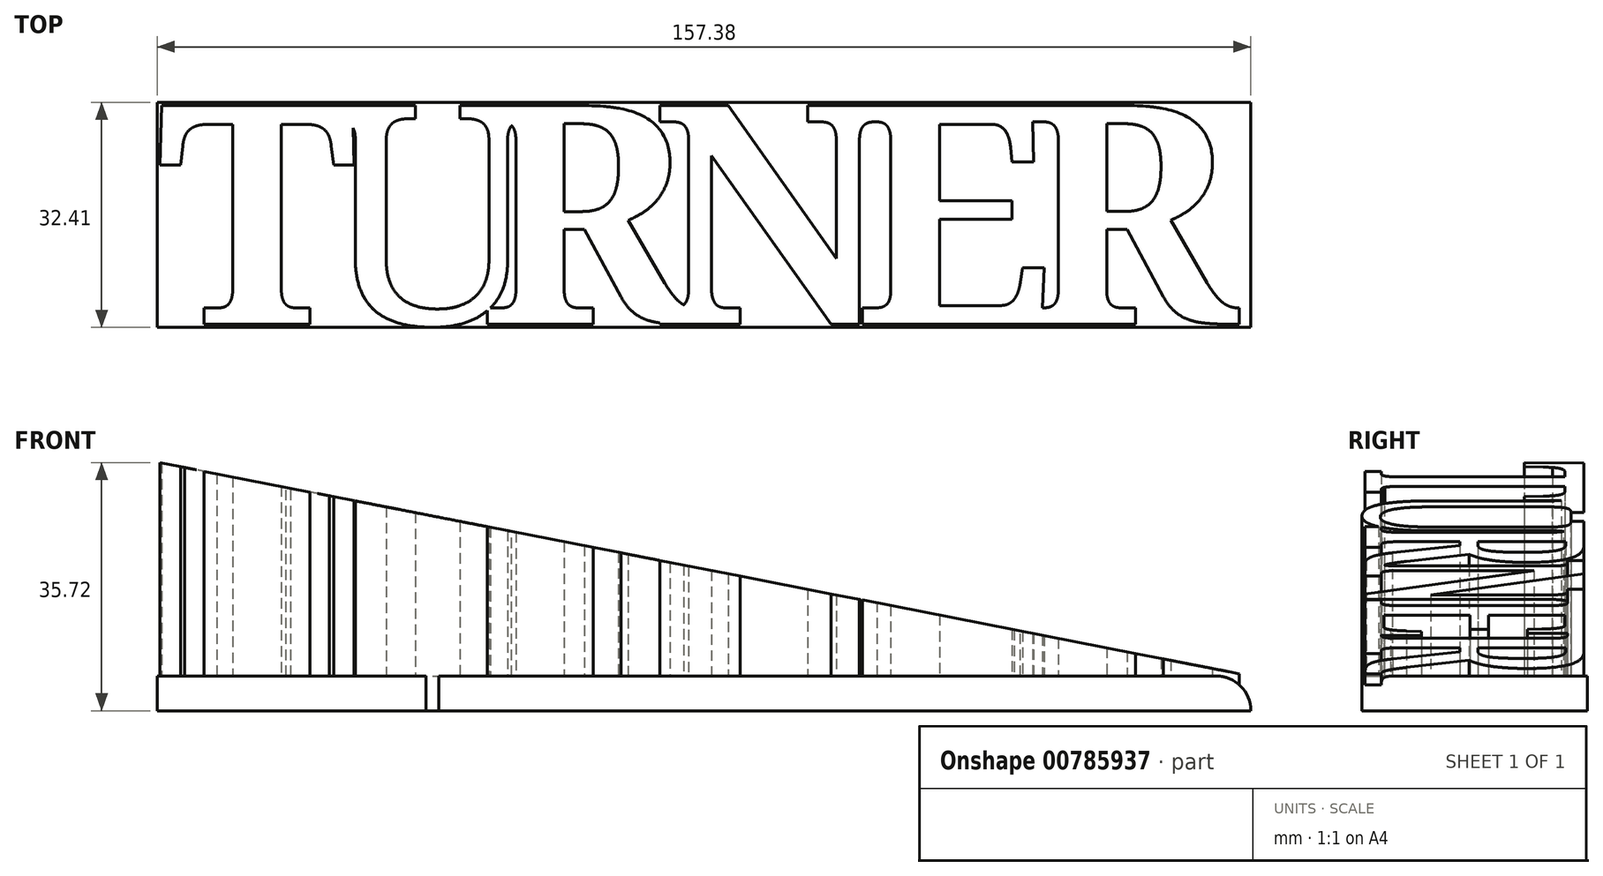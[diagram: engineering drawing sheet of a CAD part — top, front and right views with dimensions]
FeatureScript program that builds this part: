
annotation { "Feature Type Name" : "Feature", "Feature Type Description" : "" }
export const myFeature = defineFeature(function(context is Context, id is Id, definition is map)
    precondition{}
    {
        {
            var Q0;
            Q0=qCreatedBy(makeId("Top.planeOp"),FACE);
            var sketch = newSketch(context, id + "F0", { "sketchPlane" : qUnion([Q0])});
            skCircle(sketch, "E0", {"center": v(0, 0) * mm, "radius": 77 * mm, "construction": true});
            skText(sketch, "E1", { "text": "T", "fontName": "NotoSerif-Bold.ttf"});
            skText(sketch, "E2", { "text": "U", "fontName": "NotoSerif-Regular.ttf"});
            skText(sketch, "E3", { "text": "R", "fontName": "NotoSerif-Bold.ttf"});
            skText(sketch, "E4", { "text": "N", "fontName": "NotoSerif-Bold.ttf"});
            skText(sketch, "E5", { "text": "E", "fontName": "NotoSerif-Bold.ttf"});
            skText(sketch, "E6", { "text": "R", "fontName": "NotoSerif-Bold.ttf"});
            const initialGuessF0  = {"E1": [-0.07837, -0.01588, 1, 0, 0.03175], "E2": [-0.05468, -0.01588, 1, 0, 0.03175], "E3": [-0.03206, -0.01588, 1, 0, 0.03175], "E4": [-0.0072, -0.01588, 1, 0, 0.03175], "E5": [0.02189, -0.01587, 1, 0, 0.03175], "E6": [0.046, -0.01587, 1, 0, 0.03175]};
            skSetInitialGuess(sketch, initialGuessF0);
            skSolve(sketch);
        }
        {
            var Q0;
            Q0 = qSketchRegion(id + "F0", true);
            extrude(context, id + "F1", {"entities" : qUnion([Q0]), "depth" : 38.1 * mm, "offsetDistance" : 25 * mm});
        }
        {
            var Q0;
            Q0=qCreatedBy(makeId("Top.planeOp"),FACE);
            var sketch = newSketch(context, id + "F2", { "sketchPlane" : qUnion([Q0])});
            skLineSegment(sketch, "E7.bottom", {"start": v(-78.34, 16.1) * mm, "end": v(79.04, 16.1) * mm});
            skLineSegment(sketch, "E7.top", {"start": v(-78.34, -16.3) * mm, "end": v(79.04, -16.3) * mm});
            skLineSegment(sketch, "E7.left", {"start": v(-78.34, 16.1) * mm, "end": v(-78.34, -16.3) * mm});
            skLineSegment(sketch, "E7.right", {"start": v(79.04, 16.1) * mm, "end": v(79.04, -16.3) * mm});
            skSolve(sketch);
        }
        {
            var Q0;
            Q0 = qSketchRegion(id + "F2", true);
            extrude(context, id + "F3", {"entities" : qUnion([Q0]), "operationType" : NewBodyOperationType.ADD, "depth" : 5 * mm, "offsetDistance" : 25 * mm});
        }
        {
            var Q0;
            {var subQ2=sQuery(id+"F2.wireOp",EDGE,"E7.top");var subQ4=sQuery(id+"F0.wireOp",EDGE,"E2.sketch_text.stroke-45");Q0=makeQuery(id+"F3.boolean.opBoolean","SPLIT",FACE,{"disambiguationData":[TD([makeQuery(id+"F1.opExtrude","SWEPT_FACE",FACE,{"disambiguationData":[OSD([subQ4])]})])],"derivedFrom":makeQuery(id+"F3.opExtrude","SWEPT_FACE",FACE,{"disambiguationData":[OSD([subQ2])]})});}
            var sketch = newSketch(context, id + "F4", { "sketchPlane" : qUnion([Q0])});
            skPoint(sketch, "E8", {"position": v(79.04, 5) * mm});
            skLineSegment(sketch, "E9", {"start": v(79.04, 5) * mm, "end": v(-100.52, 40.14) * mm});
            skLineSegment(sketch, "E10", {"start": v(-100.52, 40.14) * mm, "end": v(79.04, 40.14) * mm});
            skLineSegment(sketch, "E11", {"start": v(79.04, 40.14) * mm, "end": v(79.04, 5) * mm});
            skSolve(sketch);
        }
        {
            var Q0;
            Q0 = qSketchRegion(id + "F4", true);
            extrude(context, id + "F5", {"entities" : qUnion([Q0]), "operationType" : NewBodyOperationType.REMOVE, "endBound" : BoundingType.SYMMETRIC, "oppositeDirection" : true, "depth" : 95.2 * mm, "offsetDistance" : 25 * mm});
        }
        {
            var Q0;
            Q0=makeQuery(id+"F3.opExtrude","CAP_EDGE",EDGE,{"disambiguationData":[OSD([sQuery(id+"F2.wireOp",EDGE,"E7.right")])],"isStart":false});
            fillet(context, id + "F6", {"entities" : qUnion([Q0]), "radius" : 5 * mm, "tangentPropagation" : true, "allowEdgeOverflow" : false});
        }
    });
